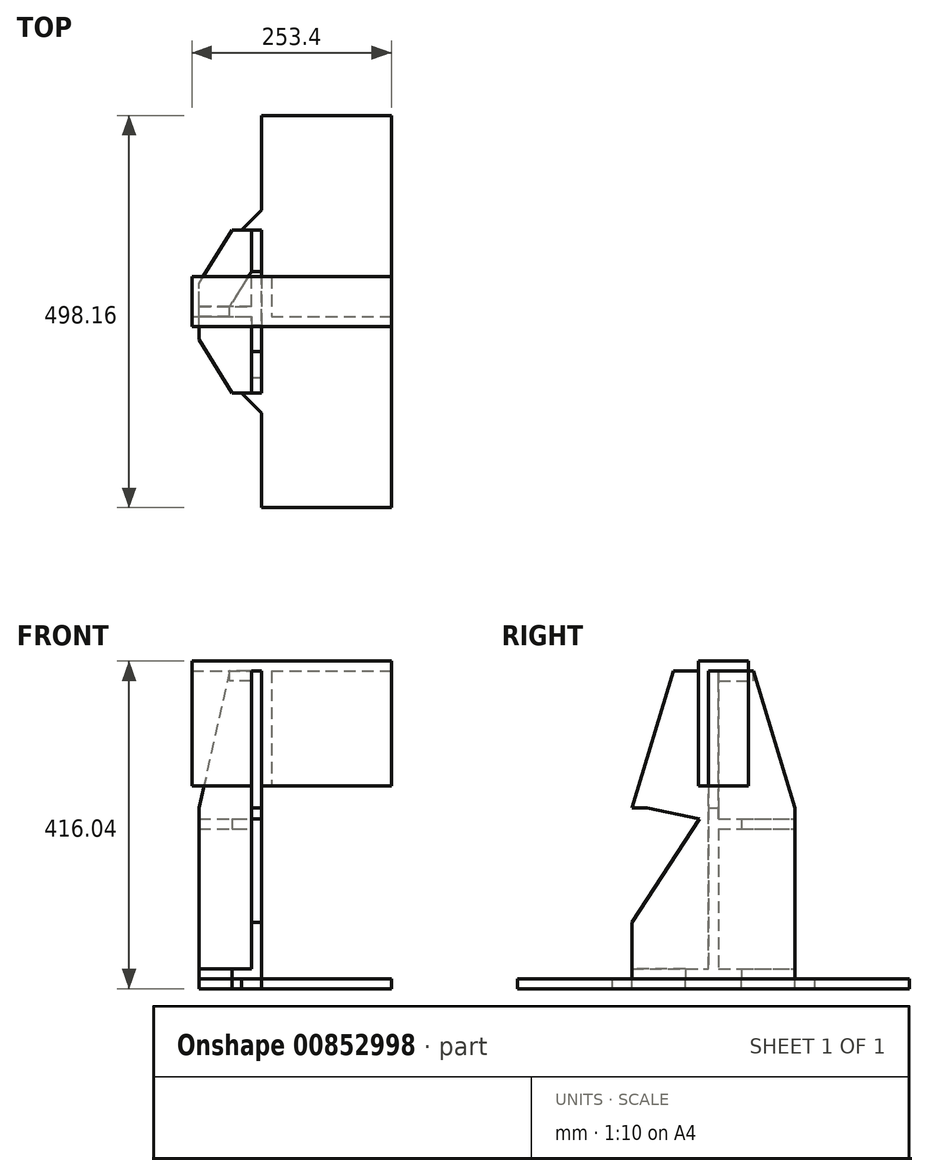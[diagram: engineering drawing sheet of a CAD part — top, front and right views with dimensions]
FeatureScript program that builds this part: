
annotation { "Feature Type Name" : "Feature", "Feature Type Description" : "" }
export const myFeature = defineFeature(function(context is Context, id is Id, definition is map)
    precondition{}
    {
        {
            var Q0;
            Q0=qCreatedBy(makeId("Top.planeOp"),FACE);
            var sketch = newSketch(context, id + "F0", { "sketchPlane" : qUnion([Q0])});
            skLineSegment(sketch, "E0", {"start": v(-244.47, 0) * mm, "end": v(-244.47, 35.8) * mm});
            skLineSegment(sketch, "E1", {"start": v(-244.47, 35.8) * mm, "end": v(-202.5, 103.72) * mm});
            skLineSegment(sketch, "E2", {"start": v(-202.5, 103.72) * mm, "end": v(-177.8, 103.72) * mm});
            skLineSegment(sketch, "E3", {"start": v(-177.8, 103.72) * mm, "end": v(-177.8, 0) * mm});
            skLineSegment(sketch, "E4.MirrorCS", {"start": v(-244.47, 0) * mm, "end": v(-244.47, -35.8) * mm});
            skLineSegment(sketch, "E5.MirrorCS", {"start": v(-244.47, -35.8) * mm, "end": v(-202.5, -103.72) * mm});
            skLineSegment(sketch, "E6.MirrorCS", {"start": v(-202.5, -103.72) * mm, "end": v(-177.8, -103.72) * mm});
            skLineSegment(sketch, "E7.MirrorCS", {"start": v(-177.8, -103.72) * mm, "end": v(-177.8, 0) * mm});
            skSolve(sketch);
        }
        {
            var Q0;
            Q0 = qSketchRegion(id + "F0", true);
            extrude(context, id + "F1", {"entities" : qUnion([Q0]), "depth" : 12.7 * mm, "offsetDistance" : 25.4 * mm});
        }
        {
            var Q0;
            Q0=makeQuery(id+"F1.opExtrude","SWEPT_FACE",FACE,{"disambiguationData":[OSD([sQuery(id+"F0.wireOp",EDGE,"E3"),sQuery(id+"F0.wireOp",EDGE,"E7.MirrorCS")])]});
            var sketch = newSketch(context, id + "F2", { "sketchPlane" : qUnion([Q0])});
            skLineSegment(sketch, "E8", {"start": v(-103.72, 0) * mm, "end": v(-103.72, 216.74) * mm});
            skLineSegment(sketch, "E9", {"start": v(-103.72, 216.74) * mm, "end": v(-51.03, 390.64) * mm});
            skLineSegment(sketch, "E10", {"start": v(-51.03, 390.64) * mm, "end": v(0, 390.64) * mm});
            skLineSegment(sketch, "E11", {"start": v(0, 390.64) * mm, "end": v(0, 0) * mm});
            skLineSegment(sketch, "E12", {"start": v(0, 0) * mm, "end": v(-103.72, 0) * mm});
            skLineSegment(sketch, "E13.MirrorCS", {"start": v(103.72, 0) * mm, "end": v(103.72, 216.74) * mm});
            skLineSegment(sketch, "E14.MirrorCS", {"start": v(0, 0) * mm, "end": v(103.72, 0) * mm});
            skLineSegment(sketch, "E15.MirrorCS", {"start": v(103.72, 216.74) * mm, "end": v(51.03, 390.64) * mm});
            skLineSegment(sketch, "E16.MirrorCS", {"start": v(51.03, 390.64) * mm, "end": v(0, 390.64) * mm});
            skSolve(sketch);
        }
        {
            var Q0;
            Q0 = qSketchRegion(id + "F2", true);
            extrude(context, id + "F3", {"entities" : qUnion([Q0]), "operationType" : NewBodyOperationType.ADD, "depth" : 12.7 * mm, "offsetDistance" : 25.4 * mm});
        }
        {
            var Q0;
            Q0=qCreatedBy(makeId("Front.planeOp"),FACE);
            var sketch = newSketch(context, id + "F4", { "sketchPlane" : qUnion([Q0])});
            skLineSegment(sketch, "E17.0", {"start": v(-177.8, 12.7) * mm, "end": v(-177.8, 216.74) * mm});
            skLineSegment(sketch, "E18.0", {"start": v(-244.47, 12.7) * mm, "end": v(-202.5, 12.7) * mm});
            skLineSegment(sketch, "E19.0", {"start": v(-202.5, 12.7) * mm, "end": v(-177.8, 12.7) * mm});
            skLineSegment(sketch, "E20.0", {"start": v(-177.8, 216.74) * mm, "end": v(-177.8, 390.64) * mm});
            skLineSegment(sketch, "E21", {"start": v(-177.8, 390.64) * mm, "end": v(-205.67, 390.64) * mm});
            skLineSegment(sketch, "E22", {"start": v(-205.67, 390.64) * mm, "end": v(-244.47, 216.74) * mm});
            skLineSegment(sketch, "E23", {"start": v(-244.47, 216.74) * mm, "end": v(-244.47, 12.7) * mm});
            skSolve(sketch);
        }
        {
            var Q0;
            Q0 = qSketchRegion(id + "F4", true);
            extrude(context, id + "F5", {"entities" : qUnion([Q0]), "operationType" : NewBodyOperationType.ADD, "depth" : 6.35 * mm, "offsetDistance" : 25.4 * mm, "hasSecondDirection" : true, "secondDirectionOppositeDirection" : true, "secondDirectionDepth" : 6.35 * mm});
        }
        {
            var Q0;
            {var subQ0=sQuery(id+"F2.wireOp",EDGE,"E8");var subQ1=sQuery(id+"F0.wireOp",EDGE,"E6.MirrorCS");var subQ3=sQuery(id+"F2.wireOp",EDGE,"E9");var subQ4=sQuery(id+"F2.wireOp",EDGE,"E16.MirrorCS");var subQ5=sQuery(id+"F2.wireOp",EDGE,"E10");Q0=makeQuery(id+"F5.boolean.opBoolean","SPLIT",FACE,{"disambiguationData":[TD([makeQuery(id+"F1.opExtrude","SWEPT_FACE",FACE,{"disambiguationData":[OSD([subQ1])]})])],"derivedFrom":makeQuery(id+"F3.opExtrude","CAP_FACE",FACE,{"disambiguationData":[OSD([subQ0,subQ3,subQ5,sQuery(id+"F2.wireOp",EDGE,"E12"),sQuery(id+"F2.wireOp",EDGE,"E13.MirrorCS"),sQuery(id+"F2.wireOp",EDGE,"E14.MirrorCS"),sQuery(id+"F2.wireOp",EDGE,"E15.MirrorCS"),subQ4])],"isStart":true})});}
            var sketch = newSketch(context, id + "F6", { "sketchPlane" : qUnion([Q0])});
            skLineSegment(sketch, "E24.0", {"start": v(6.35, 390.64) * mm, "end": v(6.35, 216.74) * mm});
            skLineSegment(sketch, "E25", {"start": v(6.35, 390.64) * mm, "end": v(6.35, 244.6) * mm});
            skLineSegment(sketch, "E26", {"start": v(6.35, 244.6) * mm, "end": v(17.48, 202.79) * mm});
            skLineSegment(sketch, "E27", {"start": v(17.48, 202.79) * mm, "end": v(84.5, 216.74) * mm});
            skLineSegment(sketch, "E28", {"start": v(84.5, 216.74) * mm, "end": v(103.72, 216.74) * mm});
            skLineSegment(sketch, "E29", {"start": v(17.48, 202.79) * mm, "end": v(103.72, 71.3) * mm});
            skSolve(sketch);
        }
        {
            var Q0;
            Q0=makeQuery(id+"F6.imprint","IMPRINT",FACE,{"disambiguationData":[TD([[makeQuery(id+"F6.imprint","IMPRINT",EDGE,{"derivedFrom":sQuery(id+"F6.wireOp",EDGE,"E25")}),-1.0]])]});
            var Q1;
            Q1=makeQuery(id+"F6.imprint","IMPRINT",FACE,{"disambiguationData":[TD([[makeQuery(id+"F6.imprint","IMPRINT",EDGE,{"derivedFrom":sQuery(id+"F6.wireOp",EDGE,"E27")}),-1.0]])]});
            extrude(context, id + "F7", {"entities" : qUnion([Q0, Q1]), "operationType" : NewBodyOperationType.REMOVE, "oppositeDirection" : true, "depth" : 25.4 * mm, "offsetDistance" : 25.4 * mm});
        }
        {
            var Q0;
            {var subQ1=sQuery(id+"F0.wireOp",EDGE,"E4.MirrorCS");var subQ2=sQuery(id+"F0.wireOp",EDGE,"E0");var subQ3=sQuery(id+"F0.wireOp",EDGE,"E2");var subQ4=sQuery(id+"F0.wireOp",EDGE,"E1");Q0=makeQuery(id+"F5.boolean.opBoolean","SPLIT",FACE,{"disambiguationData":[TD([makeQuery(id+"F1.opExtrude","SWEPT_FACE",FACE,{"disambiguationData":[OSD([subQ4])]})])],"derivedFrom":makeQuery(id+"F1.opExtrude","CAP_FACE",FACE,{"disambiguationData":[OSD([subQ2,subQ4,subQ3,sQuery(id+"F0.wireOp",EDGE,"E3"),subQ1,sQuery(id+"F0.wireOp",EDGE,"E5.MirrorCS"),sQuery(id+"F0.wireOp",EDGE,"E6.MirrorCS"),sQuery(id+"F0.wireOp",EDGE,"E7.MirrorCS")])],"isStart":false})});}
            extrude(context, id + "F8", {"entities" : qUnion([Q0]), "operationType" : NewBodyOperationType.ADD, "depth" : 190.5 * mm, "offsetDistance" : 25.4 * mm, "hasSecondDirection" : true, "secondDirectionOppositeDirection" : false, "secondDirectionDepth" : 177.8 * mm});
        }
        {
            var Q0;
            Q0=makeQuery(id+"F5.boolean.opBoolean","MERGE",FACE,{"derivedFrom":[makeQuery(id+"F3.opExtrude","SWEPT_FACE",FACE,{"disambiguationData":[OSD([sQuery(id+"F2.wireOp",EDGE,"E10"),sQuery(id+"F2.wireOp",EDGE,"E16.MirrorCS")])]}),makeQuery(id+"F5.opExtrude","SWEPT_FACE",FACE,{"disambiguationData":[OSD([sQuery(id+"F4.wireOp",EDGE,"E21")])]})]});
            var sketch = newSketch(context, id + "F9", { "sketchPlane" : qUnion([Q0])});
            skLineSegment(sketch, "E30", {"start": v(-177.8, 51.03) * mm, "end": v(-205.67, 6.35) * mm});
            skSolve(sketch);
        }
        {
            var Q0;
            Q0=makeQuery(id+"F9.imprint","IMPRINT",FACE,{"disambiguationData":[TD([[makeQuery(id+"F9.imprint","IMPRINT",EDGE,{"derivedFrom":sQuery(id+"F9.wireOp",EDGE,"E30")}),1.0]])]});
            extrude(context, id + "F10", {"entities" : qUnion([Q0]), "operationType" : NewBodyOperationType.ADD, "oppositeDirection" : true, "depth" : 12.7 * mm, "offsetDistance" : 25.4 * mm});
        }
        {
            var Q0;
            Q0=makeQuery(id+"F3.boolean.opBoolean","MERGE",FACE,{"derivedFrom":[makeQuery(id+"F1.opExtrude","CAP_FACE",FACE,{"disambiguationData":[OSD([sQuery(id+"F0.wireOp",EDGE,"E0"),sQuery(id+"F0.wireOp",EDGE,"E1"),sQuery(id+"F0.wireOp",EDGE,"E2"),sQuery(id+"F0.wireOp",EDGE,"E3"),sQuery(id+"F0.wireOp",EDGE,"E4.MirrorCS"),sQuery(id+"F0.wireOp",EDGE,"E5.MirrorCS"),sQuery(id+"F0.wireOp",EDGE,"E6.MirrorCS"),sQuery(id+"F0.wireOp",EDGE,"E7.MirrorCS")])],"isStart":true}),makeQuery(id+"F3.opExtrude","SWEPT_FACE",FACE,{"disambiguationData":[OSD([sQuery(id+"F2.wireOp",EDGE,"E12"),sQuery(id+"F2.wireOp",EDGE,"E14.MirrorCS")])]})]});
            var sketch = newSketch(context, id + "F11", { "sketchPlane" : qUnion([Q0])});
            skLineSegment(sketch, "E31.0.0", {"start": v(-165.1, 103.72) * mm, "end": v(-202.5, 103.72) * mm});
            skLineSegment(sketch, "E31.0.1", {"start": v(-202.5, 103.72) * mm, "end": v(-244.47, 35.8) * mm});
            skLineSegment(sketch, "E31.0.2", {"start": v(-244.47, 35.8) * mm, "end": v(-244.47, -35.8) * mm});
            skLineSegment(sketch, "E31.0.3", {"start": v(-244.47, -35.8) * mm, "end": v(-202.5, -103.72) * mm});
            skLineSegment(sketch, "E31.0.4", {"start": v(-202.5, -103.72) * mm, "end": v(-165.1, -103.72) * mm});
            skLineSegment(sketch, "E31.0.5", {"start": v(-165.1, -103.72) * mm, "end": v(-165.1, 103.72) * mm});
            skLineSegment(sketch, "E32", {"start": v(-165.1, 103.72) * mm, "end": v(-165.1, 249.08) * mm});
            skLineSegment(sketch, "E33", {"start": v(-165.1, 249.08) * mm, "end": v(0, 249.08) * mm});
            skLineSegment(sketch, "E34.MirrorCS", {"start": v(-165.1, -103.72) * mm, "end": v(-165.1, -249.08) * mm});
            skLineSegment(sketch, "E35.MirrorCS", {"start": v(-165.1, -249.08) * mm, "end": v(0, -249.08) * mm});
            skLineSegment(sketch, "E36", {"start": v(0, -249.08) * mm, "end": v(0, 249.08) * mm});
            skSolve(sketch);
        }
        {
            var Q0;
            Q0 = qSketchRegion(id + "F11", true);
            extrude(context, id + "F12", {"entities" : qUnion([Q0]), "depth" : 12.7 * mm, "offsetDistance" : 25.4 * mm});
        }
        {
            var Q0;
            Q0=makeQuery(id+"F12.opExtrude","SWEPT_EDGE",EDGE,{"disambiguationData":[OSD([sQuery(id+"F11.wireOp",EDGE,"E31.0.0"),sQuery(id+"F11.wireOp",EDGE,"E31.0.5"),sQuery(id+"F11.wireOp",EDGE,"E32")])]});
            var Q1;
            Q1=makeQuery(id+"F12.opExtrude","SWEPT_EDGE",EDGE,{"disambiguationData":[OSD([sQuery(id+"F11.wireOp",EDGE,"E31.0.4"),sQuery(id+"F11.wireOp",EDGE,"E31.0.5"),sQuery(id+"F11.wireOp",EDGE,"E34.MirrorCS")])]});
            chamfer(context, id + "F13", {"entities" : qUnion([Q0, Q1]), "width" : 25.4 * mm, "tangentPropagation" : true});
        }
        {
            var Q0;
            Q0=makeQuery(id+"F7.boolean.opBoolean","MERGE",FACE,{"derivedFrom":[makeQuery(id+"F5.opExtrude","CAP_FACE",FACE,{"disambiguationData":[OSD([sQuery(id+"F4.wireOp",EDGE,"E17.0"),sQuery(id+"F4.wireOp",EDGE,"E18.0"),sQuery(id+"F4.wireOp",EDGE,"E19.0"),sQuery(id+"F4.wireOp",EDGE,"E20.0"),sQuery(id+"F4.wireOp",EDGE,"E21"),sQuery(id+"F4.wireOp",EDGE,"E22"),sQuery(id+"F4.wireOp",EDGE,"E23")])],"isStart":false})],"fromTools":[makeQuery(id+"F7.opExtrude","SWEPT_FACE",FACE,{"disambiguationData":[OSD([sQuery(id+"F6.wireOp",EDGE,"E25")])]})]});
            var sketch = newSketch(context, id + "F14", { "sketchPlane" : qUnion([Q0])});
            skPoint(sketch, "E37.0", {"position": v(-165.1, 244.6) * mm});
            skPoint(sketch, "E38.0", {"position": v(-165.1, 390.64) * mm});
            skLineSegment(sketch, "E39.bottom", {"start": v(-253.4, 390.64) * mm, "end": v(0, 390.64) * mm});
            skLineSegment(sketch, "E39.top", {"start": v(-253.4, 244.6) * mm, "end": v(0, 244.6) * mm});
            skLineSegment(sketch, "E39.left", {"start": v(-253.4, 390.64) * mm, "end": v(-253.4, 244.6) * mm});
            skLineSegment(sketch, "E39.right", {"start": v(0, 390.64) * mm, "end": v(0, 244.6) * mm});
            skSolve(sketch);
        }
        {
            var Q0;
            Q0 = qSketchRegion(id + "F14", true);
            extrude(context, id + "F15", {"entities" : qUnion([Q0]), "depth" : 12.7 * mm, "offsetDistance" : 25.4 * mm});
        }
        {
            var Q0;
            Q0=makeQuery(id+"F15.opExtrude","CAP_FACE",FACE,{"disambiguationData":[OSD([sQuery(id+"F14.wireOp",EDGE,"E39.bottom"),sQuery(id+"F14.wireOp",EDGE,"E39.top"),sQuery(id+"F14.wireOp",EDGE,"E39.left"),sQuery(id+"F14.wireOp",EDGE,"E39.right")])],"isStart":true});
            var sketch = newSketch(context, id + "F16", { "sketchPlane" : qUnion([Q0])});
            skLineSegment(sketch, "E40.0", {"start": v(165.1, 390.64) * mm, "end": v(165.1, 244.6) * mm});
            skLineSegment(sketch, "E41.bottom", {"start": v(165.1, 390.64) * mm, "end": v(152.4, 390.64) * mm});
            skLineSegment(sketch, "E41.top", {"start": v(165.1, 244.6) * mm, "end": v(152.4, 244.6) * mm});
            skLineSegment(sketch, "E41.right", {"start": v(152.4, 390.64) * mm, "end": v(152.4, 244.6) * mm});
            skSolve(sketch);
        }
        {
            var Q0;
            Q0 = qSketchRegion(id + "F16", true);
            extrude(context, id + "F17", {"entities" : qUnion([Q0]), "operationType" : NewBodyOperationType.ADD, "depth" : 50.8 * mm, "offsetDistance" : 25.4 * mm});
        }
        {
            var Q0;
            Q0=makeQuery(id+"F17.boolean.opBoolean","MERGE",FACE,{"derivedFrom":[makeQuery(id+"F15.opExtrude","SWEPT_FACE",FACE,{"disambiguationData":[OSD([sQuery(id+"F14.wireOp",EDGE,"E39.bottom")])]}),makeQuery(id+"F17.opExtrude","SWEPT_FACE",FACE,{"disambiguationData":[OSD([sQuery(id+"F16.wireOp",EDGE,"E41.bottom")])]})]});
            var sketch = newSketch(context, id + "F18", { "sketchPlane" : qUnion([Q0])});
            skLineSegment(sketch, "E42.bottom", {"start": v(-253.4, -19.05) * mm, "end": v(0, -19.05) * mm});
            skLineSegment(sketch, "E42.top", {"start": v(-253.4, 44.45) * mm, "end": v(0, 44.45) * mm});
            skLineSegment(sketch, "E42.left", {"start": v(-253.4, -19.05) * mm, "end": v(-253.4, 44.45) * mm});
            skLineSegment(sketch, "E42.right", {"start": v(0, -19.05) * mm, "end": v(0, 44.45) * mm});
            skSolve(sketch);
        }
        {
            var Q0;
            Q0 = qSketchRegion(id + "F18", true);
            extrude(context, id + "F19", {"entities" : qUnion([Q0]), "operationType" : NewBodyOperationType.ADD, "depth" : 12.7 * mm, "offsetDistance" : 25.4 * mm});
        }
    });
